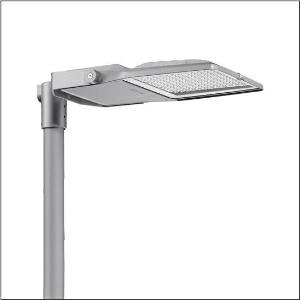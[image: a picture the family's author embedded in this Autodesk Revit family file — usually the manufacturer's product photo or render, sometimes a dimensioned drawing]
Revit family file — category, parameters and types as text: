
# Revit family: floodlight_fl_21_iq_midi___pl61_5xa7781f4c3a_8dc1
name_source: partatom
category: Lighting Fixtures
units: mm (PartAtom-declared; Revit-internal decimal feet)

## family parameters
Cut with Voids When Loaded = No
Host = Face
Light Source = No
Part Type = Normal
Room Calculation Point = No
Round Connector Dimension = Use Diameter
Shared = No

## types (1)
- --- (1 x LED, 36650 lm, 270.2 W, 4000K)
    Apparent Load = 270 VA
    CIE Flux Codes = 33 65 98 100 100
    Color Rendering = 70
    Color Temperature = 4000K
    Default Elevation = 1800 mm
    Description = Floodlight FL 21 iQ midi, floodlight, primary light control with lens, of PMMA, primary optical cover: protective disc, of toughened safety glass, transparent, light distribution: PL61, light emission: direct distribution, installation type: surface-mounted, LED, High Power LED, rated luminous flux: 36.650lm, luminous efficacy: 136lm/W, light colour: 740, colour temperature: 4000K, control gear: ECG iQ, control: optimised constant luminous flux control (CLO 2.0), Desk-Remote (wireless, voltage-free reading and setting of iQ features in the workshop via application-optimized NFC function/RFID function), Light-Fading, Smart-Wire, Night-Set, Lumen-Switch, Temp-Guard, Auto-Match, with terminal, 6-pole, mains connection: 220..240V, AC, 50/60Hz, start of lifetime: 270W, end of service life: 287W, reduction: 118W, luminaire housing, of diecast aluminium, powder-coated, Siteco® metallic grey (DB 702S), corrosivity category C5 mid according to DIN EN ISO 12944, sealing non-destructively replaceable, please order mast flange separately, mast bracket, of steel, galvanised, powder-coated, Siteco® metallic grey (DB 702S), protection rating (complete): IP66, insulation class (complete): insulation class II (safety insulation), certification: CE, protection symbol: D, impact resistance: IK08, permissible operating ambient temperature: -40..+40°C, permissible operating ambient temperature for outdoor applications: -40..+50°C, standard: DIN EN 12944, LABS conformity tested according to VDMA 24364:2018-05, packaging unit: 1 piece

Light Distribution: PL61
    Height = 76 mm
    Lamp = 1 x LED
    Lamp Light Flux = 36650 lm
    Lamp Power = 270.2 W
    Lamp count = 1
    Length = 657 mm
    Luminous efficacy = 136 lm/W
    Manufacturer = Siteco
    ModVariant = No
    Model = 5XA7781F4C3A
    Number of Poles = 1
    OnlyDefault = Yes
    Power Factor = 1
    Product Name = Floodlight FL 21 iQ midi | PL61
    Product group = floodlight | pylon annexe
    ProductGroupID = 6200
    Protection Class = Protection class II
    Protection Degree = IP 66
    RLX_Detail_Level = 1
    RLX_Emergency_Light_Flux = 0 lm
    RLX_Emergency_Type = 0
    RLX_Emergency_Type_DB = No
    RlxData = <blob elided: 153637 chars, md5=72666e73>
    Socket = socket
    Standby Power = 0 W
    System Light Flux = 36650 lm
    System Power = 270 W
    Type Comments = factory setting: luminous flux: 100 % | dim-lin: 254 | 620 mA
    Type Image = l_1007123.jpg
    URL = http://relux.com
    VarID = @adj_038539
    Voltage = 0 V
    Weight = 0.00 kg
    Width = 442 mm

## geometry (parser evidence)
native form markers: Blend x4, Sweep x14
no freeform markers — native parametric forms only
